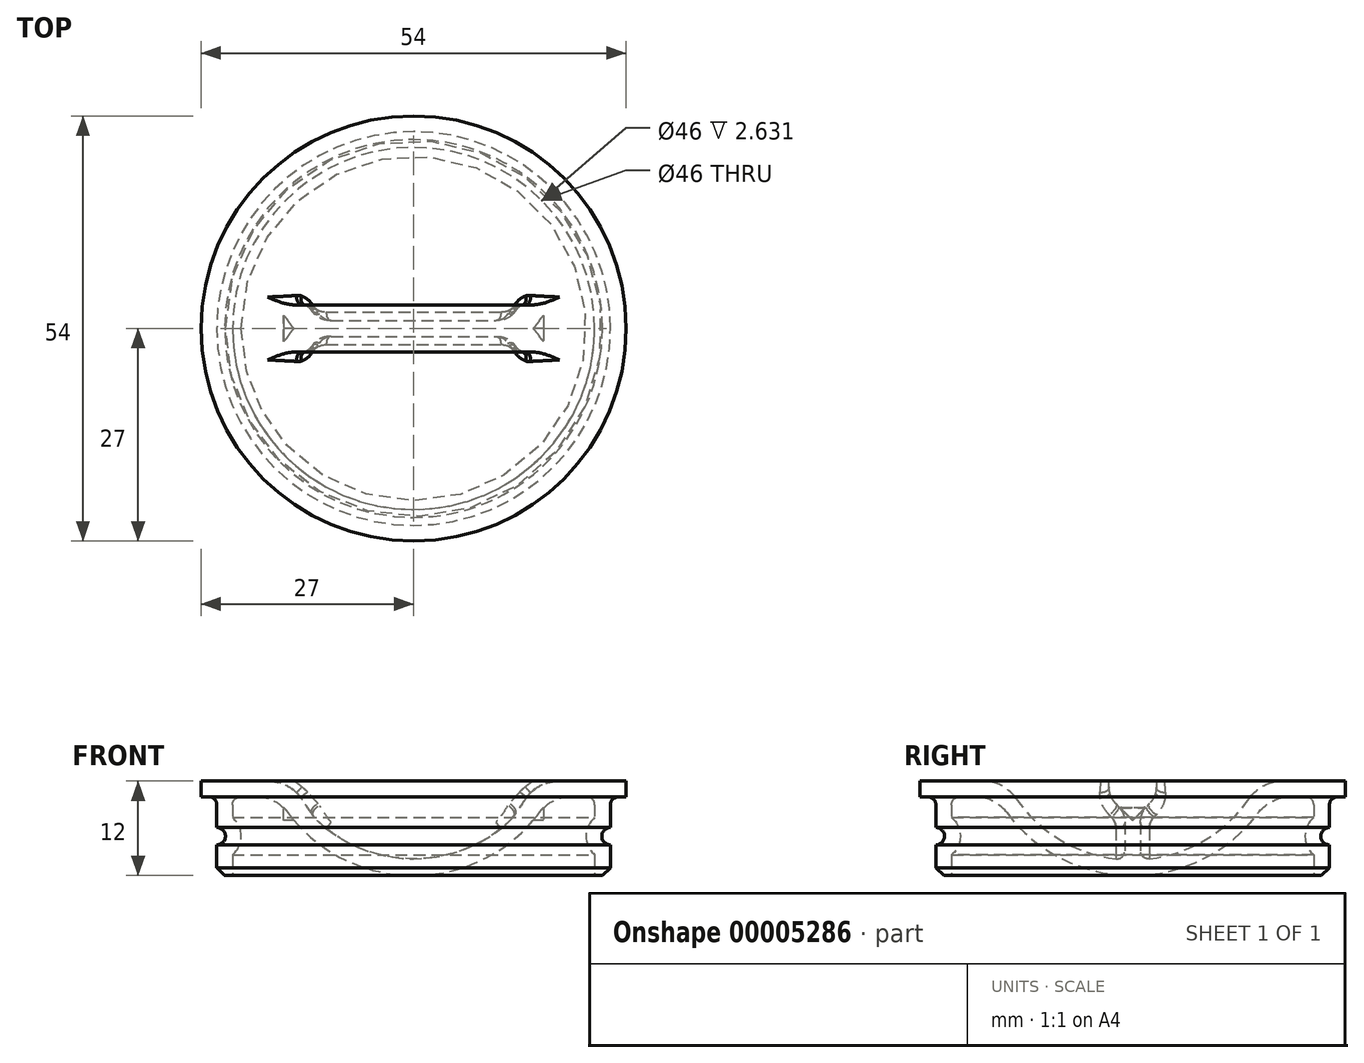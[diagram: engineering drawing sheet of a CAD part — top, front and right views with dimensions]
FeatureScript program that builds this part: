
annotation { "Feature Type Name" : "Feature", "Feature Type Description" : "" }
export const myFeature = defineFeature(function(context is Context, id is Id, definition is map)
    precondition{}
    {
        {
            var Q0;
            Q0=qCreatedBy(makeId("Front.planeOp"),FACE);
            var sketch = newSketch(context, id + "F0", { "sketchPlane" : qUnion([Q0])});
            skLineSegment(sketch, "E0", {"start": v(0, 0) * mm, "end": v(0, 58.55) * mm, "construction": true});
            skLineSegment(sketch, "E1", {"start": v(-23, 0) * mm, "end": v(-25, 0) * mm});
            skLineSegment(sketch, "E2", {"start": v(-25, 0) * mm, "end": v(-25, 3.9) * mm});
            skLineSegment(sketch, "E3", {"start": v(-25, 10) * mm, "end": v(-27, 10) * mm});
            skLineSegment(sketch, "E4", {"start": v(-27, 10) * mm, "end": v(-27, 12) * mm});
            skLineSegment(sketch, "E5", {"start": v(-27, 12) * mm, "end": v(-16.12, 12) * mm});
            skLineSegment(sketch, "E6.top", {"start": v(-23, 10) * mm, "end": v(-17.32, 10) * mm});
            skLineSegment(sketch, "E6.left", {"start": v(-23, 0) * mm, "end": v(-23, 2.63) * mm});
            skArc(sketch, "E7", {"start": v(-17.32, 10) * mm, "mid": v(-10, 2.68) * mm, "end": v(0, 0) * mm});
            skArc(sketch, "E8", {"start": v(-16.12, 12) * mm, "mid": v(-9.49, 4.7) * mm, "end": v(0, 2) * mm});
            skLineSegment(sketch, "E9", {"start": v(0, 2) * mm, "end": v(0, 0) * mm});
            skArc(sketch, "E10", {"start": v(-25, 3.9) * mm, "mid": v(-23.9, 5) * mm, "end": v(-25, 6.1) * mm});
            skLineSegment(sketch, "E11.trimOffspring", {"start": v(-25, 6.1) * mm, "end": v(-25, 10) * mm});
            skArc(sketch, "E12", {"start": v(-23, 2.63) * mm, "mid": v(-21.9, 5) * mm, "end": v(-23, 7.37) * mm});
            skLineSegment(sketch, "E13.trimOffspring", {"start": v(-23, 7.37) * mm, "end": v(-23, 10) * mm});
            skSolve(sketch);
        }
        {
            var Q0;
            Q0=makeQuery(id+"F0.imprint","IMPRINT",FACE,{"disambiguationData":[TD([[makeQuery(id+"F0.imprint","IMPRINT",EDGE,{"derivedFrom":sQuery(id+"F0.wireOp",EDGE,"E1")}),-1.0]])]});
            var Q1;
            Q1=sQuery(id+"F0.wireOp",EDGE,"E0");
            revolve(context, id + "F1", {"entities" : qUnion([Q0]), "axis" : qUnion([Q1]), "revolveType" : RevolveType.FULL});
        }
        {
            var Q0;
            Q0=qCreatedBy(makeId("Front.planeOp"),FACE);
            var sketch = newSketch(context, id + "F2", { "sketchPlane" : qUnion([Q0])});
            skLineSegment(sketch, "E14.0", {"start": v(16.12, 12) * mm, "end": v(-16.12, 12) * mm});
            skArc(sketch, "E15", {"start": v(-16.12, 12) * mm, "mid": v(0, 2) * mm, "end": v(16.12, 12) * mm});
            skSolve(sketch);
        }
        {
            var Q0;
            Q0 = qSketchRegion(id + "F2", true);
            extrude(context, id + "F3", {"entities" : qUnion([Q0]), "endBound" : BoundingType.SYMMETRIC, "depth" : 2 * mm});
        }
        {
            var Q0;
            Q0=makeQuery(id+"F3.opExtrude","SWEPT_BODY",BODY,{"disambiguationData":[OSD([sQuery(id+"F2.wireOp",EDGE,"E14.0"),sQuery(id+"F2.wireOp",EDGE,"b1fb4e6f-016a-4ef0-82b3-d27d703cc306")])]});
            var Q1;
            Q1=makeQuery(id+"F1.opRevolve","SWEPT_BODY",BODY,{"disambiguationData":[OSD([sQuery(id+"F0.wireOp",EDGE,"E1"),sQuery(id+"F0.wireOp",EDGE,"E2"),sQuery(id+"F0.wireOp",EDGE,"E3"),sQuery(id+"F0.wireOp",EDGE,"E4"),sQuery(id+"F0.wireOp",EDGE,"E5"),sQuery(id+"F0.wireOp",EDGE,"E6.top"),sQuery(id+"F0.wireOp",EDGE,"E6.left"),sQuery(id+"F0.wireOp",EDGE,"E7"),sQuery(id+"F0.wireOp",EDGE,"E8"),sQuery(id+"F0.wireOp",EDGE,"E9"),sQuery(id+"F0.wireOp",EDGE,"E10"),sQuery(id+"F0.wireOp",EDGE,"E11.trimOffspring"),sQuery(id+"F0.wireOp",EDGE,"E12"),sQuery(id+"F0.wireOp",EDGE,"E13.trimOffspring")])]});
            booleanBodies(context, id + "F4", {"operationType" : BooleanOperationType.UNION, "tools" : qUnion([Q0, Q1])});
        }
        {
            var Q0;
            Q0=makeQuery(id+"F1.opRevolve","SWEPT_EDGE",EDGE,{"disambiguationData":[OSD([sQuery(id+"F0.wireOp",EDGE,"E3"),sQuery(id+"F0.wireOp",EDGE,"E11.trimOffspring")])]});
            var Q1;
            Q1=makeQuery(id+"F1.opRevolve","SWEPT_EDGE",EDGE,{"disambiguationData":[OSD([sQuery(id+"F0.wireOp",EDGE,"E6.top"),sQuery(id+"F0.wireOp",EDGE,"E13.trimOffspring")])]});
            fillet(context, id + "F5", {"entities" : qUnion([Q0, Q1]), "radius" : 1 * mm, "tangentPropagation" : true, "allowEdgeOverflow" : false});
        }
        {
            var Q0;
            Q0=qCreatedBy(makeId("Right.planeOp"),FACE);
            var sketch = newSketch(context, id + "F6", { "sketchPlane" : qUnion([Q0])});
            skLineSegment(sketch, "E16.bottom", {"start": v(3, 12) * mm, "end": v(-3, 12) * mm});
            skLineSegment(sketch, "E16.left", {"start": v(3, 12) * mm, "end": v(3, 10) * mm});
            skLineSegment(sketch, "E16.right", {"start": v(-3, 12) * mm, "end": v(-3, 10) * mm});
            skLineSegment(sketch, "E17", {"start": v(0, 0) * mm, "end": v(0, 13.69) * mm, "construction": true});
            skLineSegment(sketch, "E18", {"start": v(3, 10) * mm, "end": v(0, 7) * mm});
            skLineSegment(sketch, "E19", {"start": v(0, 7) * mm, "end": v(-3, 10) * mm});
            skSolve(sketch);
        }
        {
            var Q0;
            Q0=makeQuery(id+"F6.imprint","IMPRINT",FACE,{"disambiguationData":[TD([[makeQuery(id+"F6.imprint","IMPRINT",EDGE,{"derivedFrom":sQuery(id+"F6.wireOp",EDGE,"E16.bottom")}),1.0]])]});
            extrude(context, id + "F7", {"entities" : qUnion([Q0]), "operationType" : NewBodyOperationType.ADD, "endBound" : BoundingType.SYMMETRIC, "depth" : 33 * mm});
        }
        {
            var Q0;
            Q0=makeQuery(id+"F7.boolean.opBoolean","INTERSECT",EDGE,{"derivedFrom":[makeQuery(id+"F3.opExtrude","CAP_FACE",FACE,{"disambiguationData":[OSD([sQuery(id+"F2.wireOp",EDGE,"E14.0"),sQuery(id+"F2.wireOp",EDGE,"E15")])],"isStart":false}),makeQuery(id+"F7.opExtrude","SWEPT_FACE",FACE,{"disambiguationData":[OSD([sQuery(id+"F6.wireOp",EDGE,"E19")])]})]});
            var Q1;
            Q1=makeQuery(id+"F7.opExtrude","SWEPT_EDGE",EDGE,{"disambiguationData":[OSD([sQuery(id+"F6.wireOp",EDGE,"E16.right"),sQuery(id+"F6.wireOp",EDGE,"E19")])]});
            var Q2;
            Q2=makeQuery(id+"F7.opExtrude","SWEPT_EDGE",EDGE,{"disambiguationData":[OSD([sQuery(id+"F6.wireOp",EDGE,"E16.left"),sQuery(id+"F6.wireOp",EDGE,"E18")])]});
            var Q3;
            Q3=makeQuery(id+"F7.boolean.opBoolean","INTERSECT",EDGE,{"derivedFrom":[makeQuery(id+"F3.opExtrude","CAP_FACE",FACE,{"disambiguationData":[OSD([sQuery(id+"F2.wireOp",EDGE,"E14.0"),sQuery(id+"F2.wireOp",EDGE,"E15")])],"isStart":true}),makeQuery(id+"F7.opExtrude","SWEPT_FACE",FACE,{"disambiguationData":[OSD([sQuery(id+"F6.wireOp",EDGE,"E18")])]})]});
            fillet(context, id + "F8", {"entities" : qUnion([Q0, Q1, Q2, Q3]), "radius" : 3 * mm, "tangentPropagation" : true, "allowEdgeOverflow" : false});
        }
        {
            var Q0;
            {var subQ0=sQuery(id+"F0.wireOp",EDGE,"E5");var subQ1=sQuery(id+"F0.wireOp",EDGE,"E8");var subQ2=sQuery(id+"F2.wireOp",EDGE,"E14.0");Q0=makeQuery(id+"F4.opBoolean","SPLIT",EDGE,{"disambiguationData":[TD([makeQuery(id+"F3.opExtrude","CAP_FACE",FACE,{"disambiguationData":[OSD([subQ2,sQuery(id+"F2.wireOp",EDGE,"E15")])],"isStart":true})])],"derivedFrom":makeQuery(id+"F1.opRevolve","SWEPT_EDGE",EDGE,{"disambiguationData":[OSD([subQ0,subQ1])]})});}
            var Q1;
            {var subQ0=sQuery(id+"F0.wireOp",EDGE,"E5");var subQ1=sQuery(id+"F0.wireOp",EDGE,"E8");var subQ2=sQuery(id+"F2.wireOp",EDGE,"E14.0");Q1=makeQuery(id+"F4.opBoolean","SPLIT",EDGE,{"disambiguationData":[TD([makeQuery(id+"F3.opExtrude","CAP_FACE",FACE,{"disambiguationData":[OSD([subQ2,sQuery(id+"F2.wireOp",EDGE,"E15")])],"isStart":false})])],"derivedFrom":makeQuery(id+"F1.opRevolve","SWEPT_EDGE",EDGE,{"disambiguationData":[OSD([subQ0,subQ1])]})});}
            var Q2;
            Q2=makeQuery(id+"F1.opRevolve","SWEPT_EDGE",EDGE,{"disambiguationData":[OSD([sQuery(id+"F0.wireOp",EDGE,"E6.top"),sQuery(id+"F0.wireOp",EDGE,"E7")])]});
            fillet(context, id + "F9", {"entities" : qUnion([Q0, Q1, Q2]), "radius" : 5 * mm, "tangentPropagation" : true, "allowEdgeOverflow" : false});
        }
        {
            var Q0;
            Q0=makeQuery(id+"F4.opBoolean","INTERSECT",EDGE,{"derivedFrom":[makeQuery(id+"F1.opRevolve","SWEPT_FACE",FACE,{"disambiguationData":[OSD([sQuery(id+"F0.wireOp",EDGE,"E8")])]}),makeQuery(id+"F3.opExtrude","CAP_FACE",FACE,{"disambiguationData":[OSD([sQuery(id+"F2.wireOp",EDGE,"E14.0"),sQuery(id+"F2.wireOp",EDGE,"E15")])],"isStart":false})]});
            var Q1;
            Q1=makeQuery(id+"F4.opBoolean","INTERSECT",EDGE,{"derivedFrom":[makeQuery(id+"F1.opRevolve","SWEPT_FACE",FACE,{"disambiguationData":[OSD([sQuery(id+"F0.wireOp",EDGE,"E8")])]}),makeQuery(id+"F3.opExtrude","CAP_FACE",FACE,{"disambiguationData":[OSD([sQuery(id+"F2.wireOp",EDGE,"E14.0"),sQuery(id+"F2.wireOp",EDGE,"E15")])],"isStart":true})]});
            fillet(context, id + "F10", {"entities" : qUnion([Q0, Q1]), "radius" : 1 * mm, "tangentPropagation" : true, "allowEdgeOverflow" : false});
        }
        {
            var Q0;
            Q0=makeQuery(id+"F1.opRevolve","SWEPT_EDGE",EDGE,{"disambiguationData":[OSD([sQuery(id+"F0.wireOp",EDGE,"E1"),sQuery(id+"F0.wireOp",EDGE,"E2")])]});
            chamfer(context, id + "F11", {"entities" : qUnion([Q0]), "width" : 1 * mm, "tangentPropagation" : true});
        }
    });
